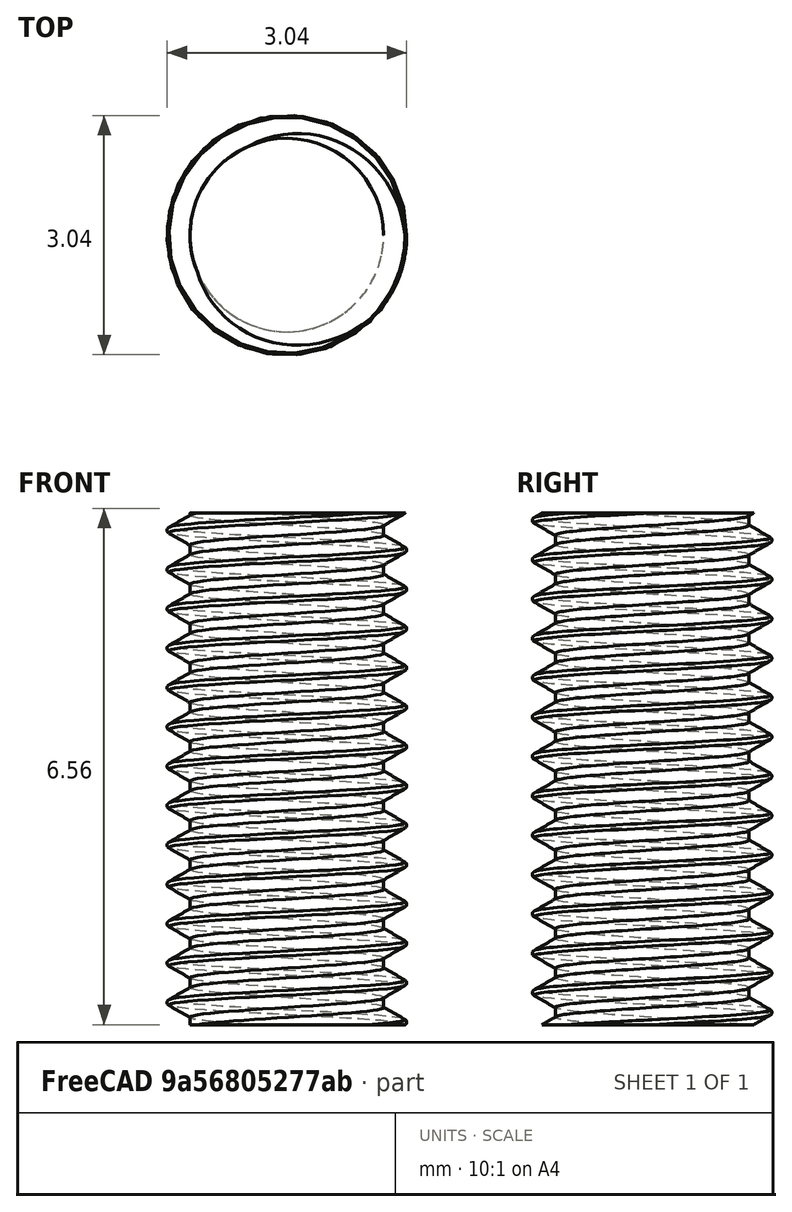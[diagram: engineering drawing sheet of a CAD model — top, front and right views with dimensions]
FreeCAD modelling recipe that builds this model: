
FCSTD DOCUMENT  (FreeCAD 0.17R13541 (Git))
Label: m3x6
License: All rights reserved
LicenseURL: http://fr.wikipedia.org/wiki/<copyright redacted>
objects: Part::FeaturePython×1, Part::Feature×1, Sketcher::SketchObject×1, PartDesign::Body×1
note: 4 computed .brp shape members not serialized (recipe doc carries the construction recipe); baked Part::Feature solids carry a one-line shape summary decoded from their .brp

FEATURE [Part::FeaturePython] ScrewTap  label="M3x6.0-ScrewTap"  # Fasteners workbench fastener (typed FeaturePython)
  diameter = 4
  invert = false
  length = 6
  matchOuter = false
  offset = 0
  thread = true
FEATURE [Part::Feature] ScrewTap001  label="M3x6.0-ScrewTap001"
  shape: bbox 4.303 x 4.617 x 7.5 mm, 58 faces (baked)
FEATURE [Sketcher::SketchObject] Sketch
  MapMode = 5
  Placement = pos=(0,0,0) rot=(1,0,0;1.5708rad)
  Support = -> [XZ_Plane001]
  sketch-geometry (27):
    g0: LineSegment StartX=0 StartY=0 StartZ=0 EndX=1.80829 EndY=0 EndZ=0
    g1: LineSegment StartX=1.80829 StartY=0 StartZ=0 EndX=1.11699 EndY=-0.399123 EndZ=0
    g2: LineSegment StartX=1.11699 StartY=-0.399123 StartZ=0 EndX=1.55 EndY=-0.649123 EndZ=0
    g3: LineSegment StartX=1.55 StartY=-0.649123 StartZ=0 EndX=1.11699 EndY=-0.899123 EndZ=0
    g4: LineSegment StartX=1.11699 StartY=-0.899123 StartZ=0 EndX=1.55 EndY=-1.14912 EndZ=0
    g5: LineSegment StartX=1.55 StartY=-1.14912 StartZ=0 EndX=1.11699 EndY=-1.39912 EndZ=0
    g6: LineSegment StartX=1.11699 StartY=-1.39912 StartZ=0 EndX=1.55 EndY=-1.64912 EndZ=0
    g7: LineSegment StartX=1.55 StartY=-1.64912 StartZ=0 EndX=1.11699 EndY=-1.89912 EndZ=0
    g8: LineSegment StartX=1.11699 StartY=-1.89912 StartZ=0 EndX=1.55 EndY=-2.14912 EndZ=0
    g9: LineSegment StartX=1.55 StartY=-2.14912 StartZ=0 EndX=1.11699 EndY=-2.39912 EndZ=0
    g10: LineSegment StartX=1.11699 StartY=-2.39912 StartZ=0 EndX=1.55 EndY=-2.64912 EndZ=0
    g11: LineSegment StartX=1.55 StartY=-2.64912 StartZ=0 EndX=1.11699 EndY=-2.89912 EndZ=0
    g12: LineSegment StartX=1.11699 StartY=-2.89912 StartZ=0 EndX=1.55 EndY=-3.14912 EndZ=0
    g13: LineSegment StartX=1.55 StartY=-3.14912 StartZ=0 EndX=1.11699 EndY=-3.39912 EndZ=0
    g14: LineSegment StartX=1.11699 StartY=-3.39912 StartZ=0 EndX=1.55 EndY=-3.64912 EndZ=0
    g15: LineSegment StartX=1.55 StartY=-3.64912 StartZ=0 EndX=1.11699 EndY=-3.89912 EndZ=0
    g16: LineSegment StartX=1.11699 StartY=-3.89912 StartZ=0 EndX=1.55 EndY=-4.14912 EndZ=0
    g17: LineSegment StartX=1.55 StartY=-4.14912 StartZ=0 EndX=1.11699 EndY=-4.39912 EndZ=0
    g18: LineSegment StartX=1.11699 StartY=-4.39912 StartZ=0 EndX=1.55 EndY=-4.64912 EndZ=0
    g19: LineSegment StartX=1.55 StartY=-4.64912 StartZ=0 EndX=1.11699 EndY=-4.89912 EndZ=0
    g20: LineSegment StartX=1.11699 StartY=-4.89912 StartZ=0 EndX=1.55 EndY=-5.14912 EndZ=0
    g21: LineSegment StartX=1.55 StartY=-5.14912 StartZ=0 EndX=1.11699 EndY=-5.39912 EndZ=0
    g22: LineSegment StartX=1.11699 StartY=-5.39912 StartZ=0 EndX=1.55 EndY=-5.64912 EndZ=0
    g23: LineSegment StartX=1.55 StartY=-5.64912 StartZ=0 EndX=1.11699 EndY=-5.89912 EndZ=0
    g24: LineSegment StartX=1.11699 StartY=-5.89912 StartZ=0 EndX=1.55 EndY=-6.14912 EndZ=0
    g25: LineSegment StartX=1.55 StartY=-6.14912 StartZ=0 EndX=1.11699 EndY=-6.39912 EndZ=0
    g26: LineSegment StartX=1.11699 StartY=-6.39912 StartZ=0 EndX=1.5466 EndY=-6.64716 EndZ=0
  constraints (79):
    c: Coincident(g-1,g0)
    c: Horizontal(g0)
    c: Coincident(g0,g1)
    c: Angle(g2,g1) = 1.0472
    c: Coincident(g1,g2)
    c: Coincident(g3,g2)
    c: Angle(g2,g3) = 1.0472
    c: Coincident(g4,g3)
    c: Angle(g4,g3) = 1.0472
    c: Vertical(g4,g2)
    c: DistanceY(g3,g1) = 0.5
    c: Vertical(g3,g1)
    c: Angle(g0,g1) = 0.523599
    c: DistanceX(g-1,g2) = 1.55
    c: Coincident(g4,g5)
    c: Coincident(g5,g6)
    c: Coincident(g6,g7)
    c: Coincident(g7,g8)
    c: Coincident(g8,g9)
    c: Coincident(g9,g10)
    c: Coincident(g10,g11)
    c: Coincident(g11,g12)
    c: Coincident(g12,g13)
    c: Coincident(g13,g14)
    c: Coincident(g14,g15)
    c: Coincident(g15,g16)
    c: Coincident(g16,g17)
    c: Coincident(g17,g18)
    c: Coincident(g18,g19)
    c: Coincident(g19,g20)
    c: Coincident(g20,g21)
    c: Coincident(g21,g22)
    c: Coincident(g22,g23)
    c: Coincident(g23,g24)
    c: Coincident(g24,g25)
    c: Coincident(g25,g26)
    c: Angle(g4,g5) = 1.0472
    c: Angle(g6,g5) = 1.0472
    c: Angle(g6,g7) = 1.0472
    c: Angle(g8,g7) = 1.0472
    c: Angle(g8,g9) = 1.0472
    c: Angle(g10,g9) = 1.0472
    c: Angle(g10,g11) = 1.0472
    c: Angle(g12,g11) = 1.0472
    c: Angle(g12,g13) = 1.0472
    c: Angle(g14,g13) = 1.0472
    c: Angle(g14,g15) = 1.0472
    c: Angle(g16,g15) = 1.0472
    c: Angle(g16,g17) = 1.0472
    c: Angle(g18,g17) = 1.0472
    c: Angle(g18,g19) = 1.0472
    c: Angle(g20,g19) = 1.0472
    c: Angle(g20,g21) = 1.0472
    c: Angle(g22,g21) = 1.0472
    c: Angle(g22,g23) = 1.0472
    c: Angle(g24,g23) = 1.0472
    c: Angle(g24,g25) = 1.0472
    c: Angle(g26,g25) = 1.0472
    c: Vertical(g4,g6)
    c: Vertical(g6,g8)
    c: Vertical(g8,g10)
    c: Vertical(g10,g12)
    c: Vertical(g12,g14)
    c: Vertical(g14,g16)
    c: Vertical(g16,g18)
    c: Vertical(g18,g20)
    c: Vertical(g20,g22)
    c: Vertical(g22,g24)
    c: Vertical(g3,g5)
    c: Vertical(g5,g7)
    c: Vertical(g7,g9)
    c: Vertical(g9,g11)
    c: Vertical(g11,g13)
    c: Vertical(g13,g15)
    c: Vertical(g15,g17)
    c: Vertical(g17,g19)
    c: Vertical(g19,g21)
    c: Vertical(g21,g23)
    c: Vertical(g23,g25)
FEATURE [PartDesign::Body] Body
  Group = -> [Sketch]
  Origin = -> Origin001
